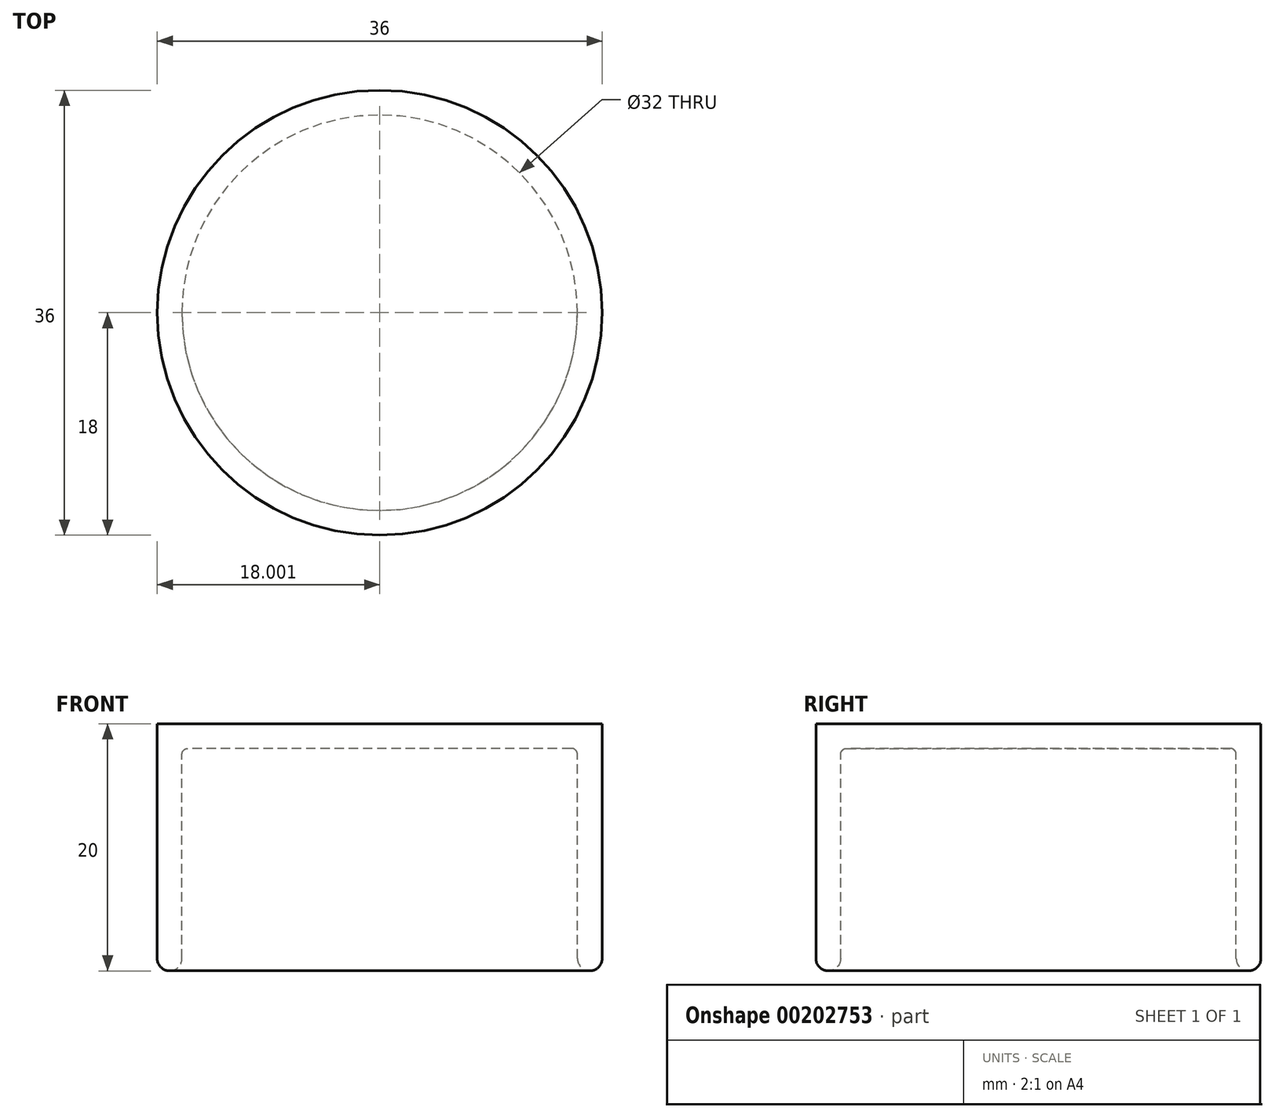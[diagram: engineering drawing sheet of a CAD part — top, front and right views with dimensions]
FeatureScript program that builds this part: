
annotation { "Feature Type Name" : "Feature", "Feature Type Description" : "" }
export const myFeature = defineFeature(function(context is Context, id is Id, definition is map)
    precondition{}
    {
        {
            var Q0;
            Q0=qCreatedBy(makeId("Front.planeOp"),FACE);
            var sketch = newSketch(context, id + "F0", { "sketchPlane" : qUnion([Q0])});
            skLineSegment(sketch, "E0.top", {"start": v(-8.9, -21.44) * mm, "end": v(-6.9, -21.44) * mm});
            skLineSegment(sketch, "E0.left", {"start": v(-8.9, -1.44) * mm, "end": v(-8.9, -21.44) * mm});
            skLineSegment(sketch, "E1", {"start": v(9.1, -1.44) * mm, "end": v(-8.9, -1.44) * mm});
            skLineSegment(sketch, "E2", {"start": v(9.1, -1.44) * mm, "end": v(9.1, -3.44) * mm});
            skLineSegment(sketch, "E3", {"start": v(9.1, -3.44) * mm, "end": v(-6.9, -3.44) * mm});
            skLineSegment(sketch, "E4", {"start": v(-6.9, -3.44) * mm, "end": v(-6.9, -21.44) * mm});
            skSolve(sketch);
        }
        {
            var Q0;
            Q0 = qSketchRegion(id + "F0", true);
            var Q1;
            Q1=sQuery(id+"F0.wireOp",EDGE,"E2");
            revolve(context, id + "F1", {"entities" : qUnion([Q0]), "axis" : qUnion([Q1]), "revolveType" : RevolveType.FULL});
        }
        {
            var Q0;
            Q0=makeQuery(id+"F1.opRevolve","SWEPT_FACE",FACE,{"disambiguationData":[OSD([sQuery(id+"F0.wireOp",EDGE,"E3")])]});
            fillet(context, id + "F2", {"entities" : qUnion([Q0]), "radius" : 0.5 * mm, "tangentPropagation" : true, "allowEdgeOverflow" : false});
        }
        {
            var Q0;
            Q0=makeQuery(id+"F1.opRevolve","SWEPT_FACE",FACE,{"disambiguationData":[OSD([sQuery(id+"F0.wireOp",EDGE,"E0.top")])]});
            fillet(context, id + "F3", {"entities" : qUnion([Q0]), "radius" : 1 * mm, "tangentPropagation" : true, "allowEdgeOverflow" : false});
        }
    });
